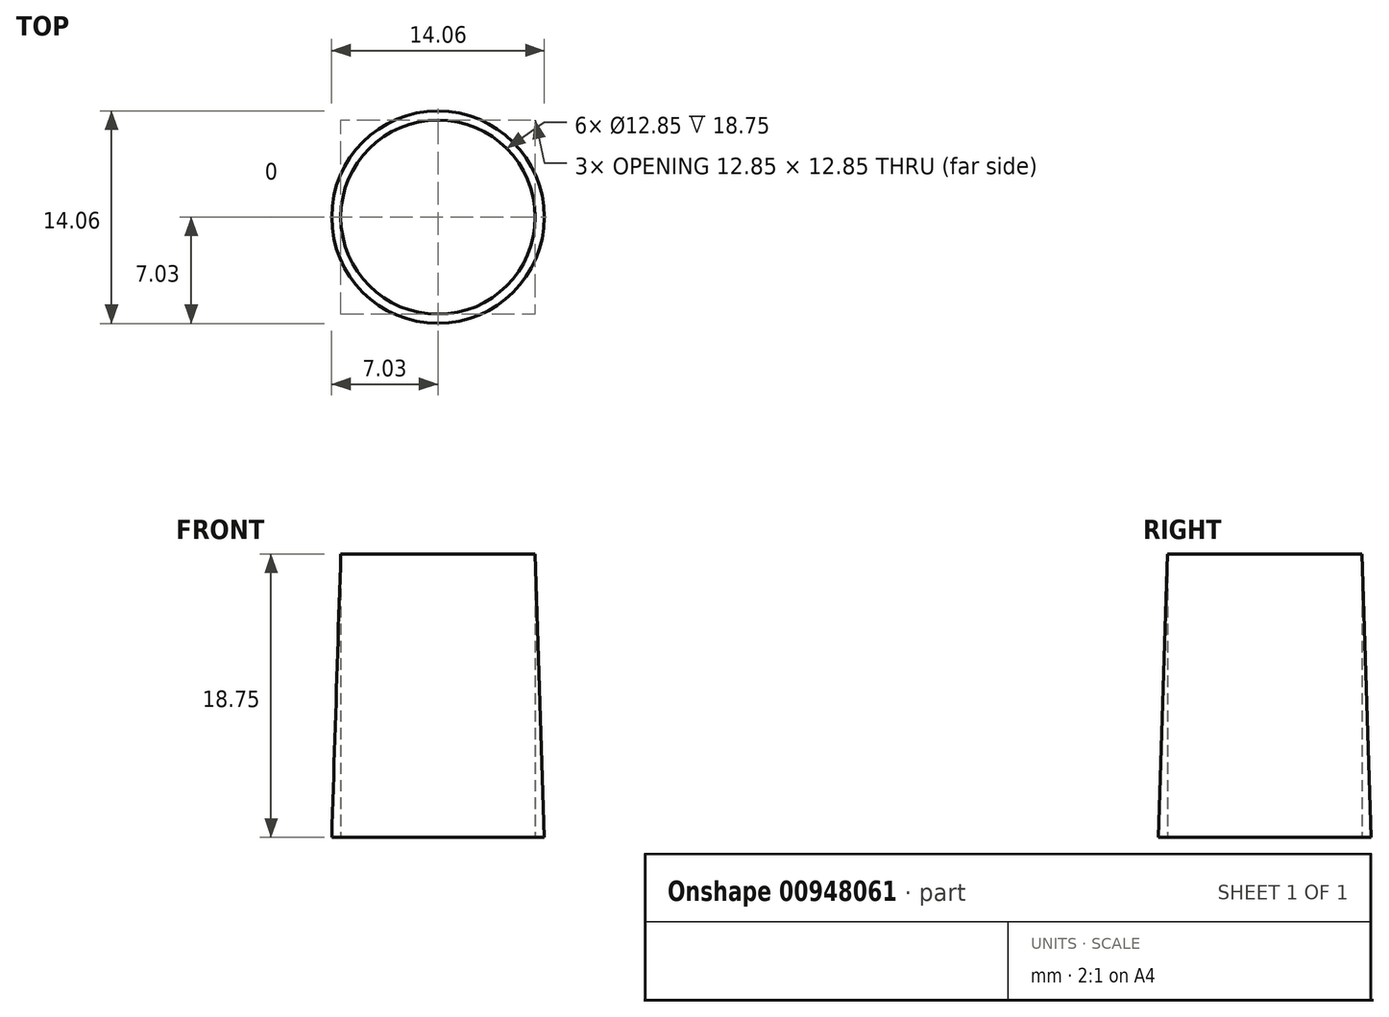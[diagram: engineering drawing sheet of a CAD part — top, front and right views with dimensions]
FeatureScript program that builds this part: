
annotation { "Feature Type Name" : "Feature", "Feature Type Description" : "" }
export const myFeature = defineFeature(function(context is Context, id is Id, definition is map)
    precondition{}
    {
        {
            var Q0;
            Q0=qCreatedBy(makeId("Top.planeOp"),FACE);
            var sketch = newSketch(context, id + "F0", { "sketchPlane" : qUnion([Q0])});
            skCircle(sketch, "E0", {"center": v(0, 0) * mm, "radius": 7.03 * mm});
            skCircle(sketch, "E1", {"center": v(0, 0) * mm, "radius": 6.42 * mm});
            skSolve(sketch);
        }
        {
            var Q0;
            Q0=makeQuery(id+"F0.imprint","IMPRINT",FACE,{"disambiguationData":[TD([[makeQuery(id+"F0.imprint","IMPRINT",EDGE,{"derivedFrom":sQuery(id+"F0.wireOp",EDGE,"E0")}),1.0]])]});
            extrude(context, id + "F1", {"entities" : qUnion([Q0]), "depth" : 25 * mm, "offsetDistance" : 25 * mm});
        }
        {
            var Q0;
            Q0=qCreatedBy(makeId("Front.planeOp"),FACE);
            var sketch = newSketch(context, id + "F2", { "sketchPlane" : qUnion([Q0])});
            skLineSegment(sketch, "E2", {"start": v(7.02, 25) * mm, "end": v(7.02, 0) * mm});
            skLineSegment(sketch, "E3", {"start": v(7.02, 25) * mm, "end": v(6.22, 25) * mm});
            skLineSegment(sketch, "E4", {"start": v(6.22, 25) * mm, "end": v(7.03, 0) * mm});
            skSolve(sketch);
        }
        {
            var Q0;
            Q0=makeQuery(id+"F2.imprint","IMPRINT",FACE,{"disambiguationData":[TD([[makeQuery(id+"F2.imprint","IMPRINT",EDGE,{"derivedFrom":sQuery(id+"F2.wireOp",EDGE,"E2")}),-1.0]])]});
            var Q1;
            Q1=makeQuery(id+"F1.opExtrude","CAP_EDGE",EDGE,{"disambiguationData":[OSD([sQuery(id+"F0.wireOp",EDGE,"E0")])],"isStart":true});
            revolve(context, id + "F3", {"operationType" : NewBodyOperationType.REMOVE, "surfaceOperationType" : NewSurfaceOperationType.NEW, "entities" : qUnion([Q0]), "axis" : qUnion([Q1]), "revolveType" : RevolveType.FULL, "oppositeDirection" : true});
        }
    });
